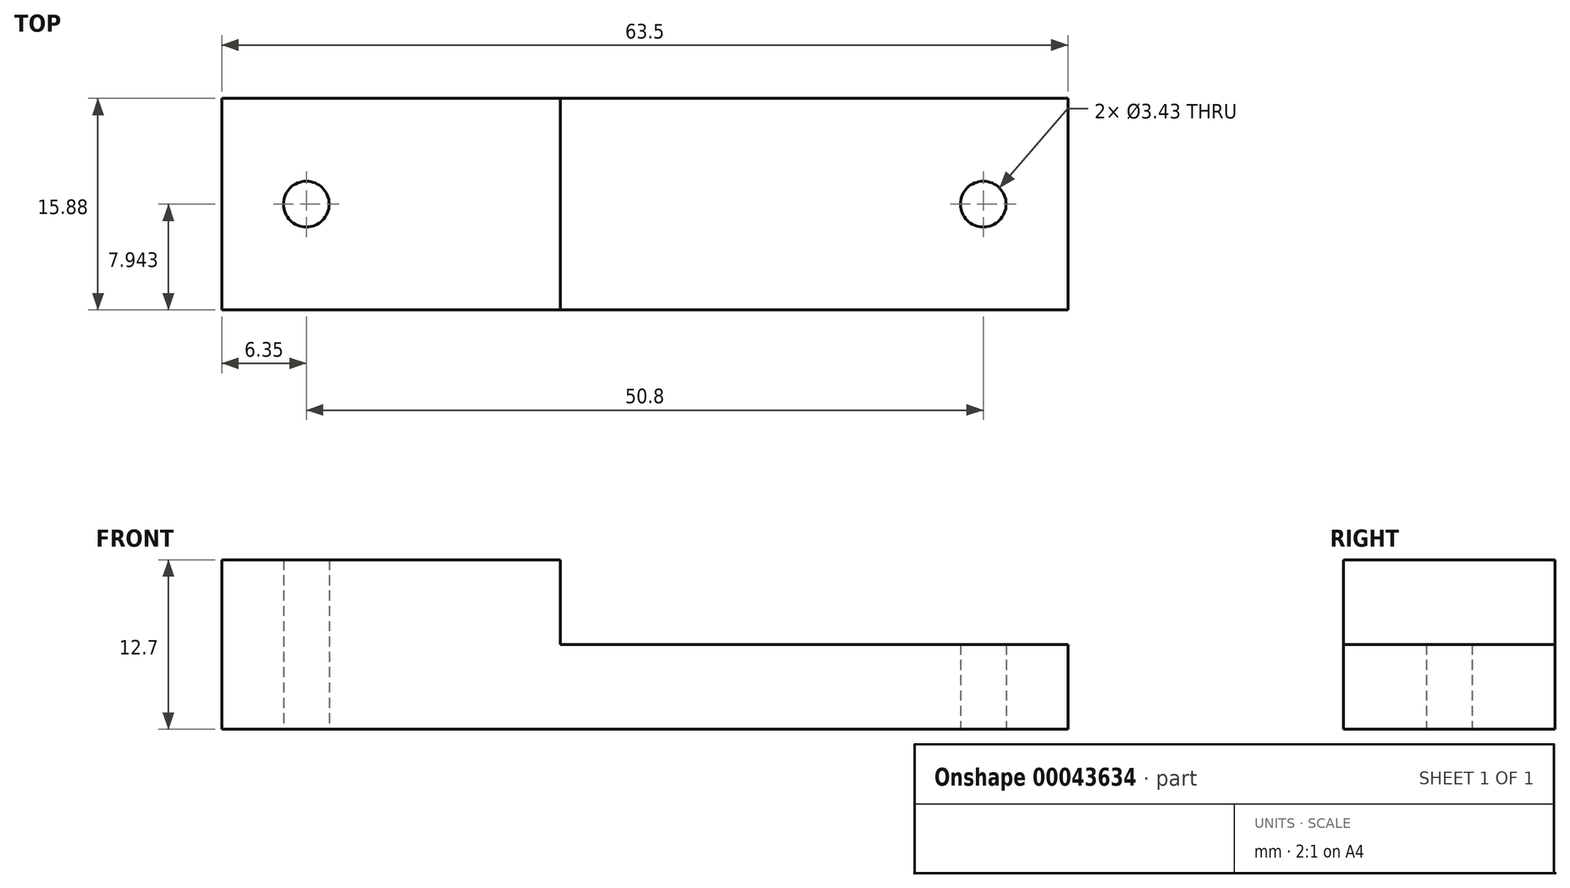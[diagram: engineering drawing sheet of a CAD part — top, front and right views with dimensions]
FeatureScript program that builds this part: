
annotation { "Feature Type Name" : "Feature", "Feature Type Description" : "" }
export const myFeature = defineFeature(function(context is Context, id is Id, definition is map)
    precondition{}
    {
        {
            var Q0;
            Q0=qCreatedBy(makeId("Front.planeOp"),FACE);
            var sketch = newSketch(context, id + "F0", { "sketchPlane" : qUnion([Q0])});
            skLineSegment(sketch, "E0", {"start": v(0, 0) * mm, "end": v(0, 12.7) * mm});
            skLineSegment(sketch, "E1", {"start": v(0, 12.7) * mm, "end": v(25.4, 12.7) * mm});
            skLineSegment(sketch, "E2", {"start": v(25.4, 12.7) * mm, "end": v(25.4, 6.35) * mm});
            skLineSegment(sketch, "E3", {"start": v(25.4, 6.35) * mm, "end": v(63.5, 6.35) * mm});
            skLineSegment(sketch, "E4", {"start": v(63.5, 6.35) * mm, "end": v(63.5, 0) * mm});
            skLineSegment(sketch, "E5", {"start": v(63.5, 0) * mm, "end": v(0, 0) * mm});
            skSolve(sketch);
        }
        {
            var Q0;
            Q0=makeQuery(id+"F0.imprint","IMPRINT",FACE,{"disambiguationData":[TD([[makeQuery(id+"F0.imprint","IMPRINT",EDGE,{"derivedFrom":sQuery(id+"F0.wireOp",EDGE,"E0")}),-1.0]])]});
            extrude(context, id + "F1", {"entities" : qUnion([Q0]), "depth" : 15.88 * mm});
        }
        {
            var Q0;
            Q0=makeQuery(id+"F1.opExtrude","SWEPT_FACE",FACE,{"disambiguationData":[OSD([sQuery(id+"F0.wireOp",EDGE,"E5")])]});
            var sketch = newSketch(context, id + "F2", { "sketchPlane" : qUnion([Q0])});
            skCircle(sketch, "E6", {"center": v(6.35, 7.94) * mm, "radius": 1.71 * mm});
            skCircle(sketch, "E7", {"center": v(57.15, 7.94) * mm, "radius": 1.71 * mm});
            skSolve(sketch);
        }
        {
            var Q0;
            Q0 = qSketchRegion(id + "F2", true);
            extrude(context, id + "F3", {"entities" : qUnion([Q0]), "operationType" : NewBodyOperationType.REMOVE, "endBound" : BoundingType.THROUGH_ALL, "oppositeDirection" : true, "depth" : 25.4 * mm});
        }
    });
